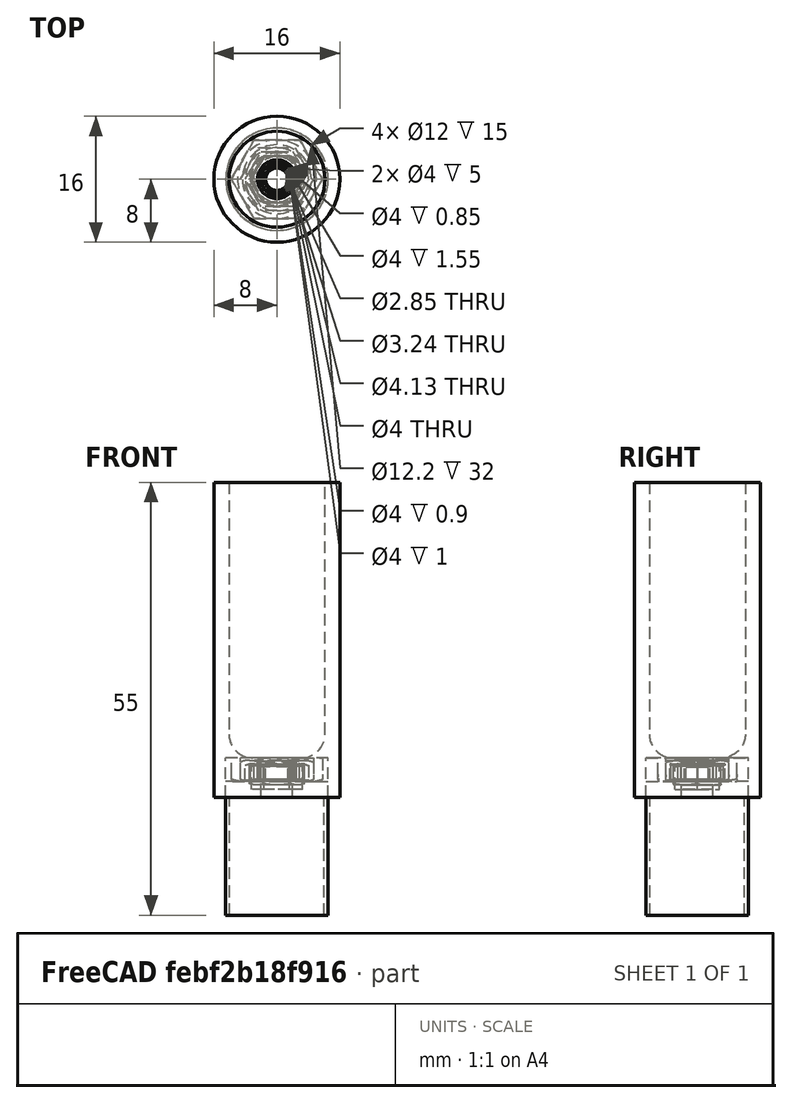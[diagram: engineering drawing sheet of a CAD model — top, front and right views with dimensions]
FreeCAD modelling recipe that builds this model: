
FCSTD DOCUMENT  (FreeCAD 0.20R29177 (Git))
Label: soporte
License: All rights reserved
LicenseURL: http://en.wikipedia.org/wiki/All_rights_reserved
objects: Part::Cylinder×24, Part::Cut×18, Part::FeaturePython×13, Part::MultiFuse×11, Mesh::Feature×6, Part::Prism×1, Part::Fillet×1
note: 68 computed .brp shape members not serialized (recipe doc carries the construction recipe); baked Part::Feature solids carry a one-line shape summary decoded from their .brp

FEATURE [Part::Cylinder] Cylinder
  Angle = 360
  AttacherType = Attacher::AttachEngine3D
  FirstAngle = 0
  Height = 15
  Radius = 6.5
  SecondAngle = 0
FEATURE [Part::Cylinder] Cylinder001
  Angle = 360
  AttacherType = Attacher::AttachEngine3D
  FirstAngle = 0
  Height = 15
  Radius = 6
  SecondAngle = 0
FEATURE [Part::Cut] Cut
  Base = -> Cylinder
  Placement = pos=(0,0,-15) rot=(0,0,1;0rad)
  Tool = -> Cylinder001
FEATURE [Part::Cylinder] Cylinder002
  Angle = 360
  AttacherType = Attacher::AttachEngine3D
  FirstAngle = 0
  Height = 5
  Radius = 6.5
  SecondAngle = 0
FEATURE [Part::Cylinder] Cylinder003
  Angle = 360
  AttacherType = Attacher::AttachEngine3D
  FirstAngle = 0
  Height = 10
  Radius = 2
  SecondAngle = 0
FEATURE [Part::Cut] Cut001
  Base = -> Cylinder002
  Tool = -> Cylinder003
FEATURE [Part::FeaturePython] Nut  label="(M3.5)-Nut"  # Fasteners workbench fastener (typed FeaturePython)
  Placement = pos=(0,0,2) rot=(0,0,1;0rad)
  diameter = 5
  invert = false
  leftHanded = false
  matchOuter = false
  offset = 0
  thread = false
  type = 11
FEATURE [Part::FeaturePython] Nut001  label="(M3.5)-Nut001"  # Fasteners workbench fastener (typed FeaturePython)
  Placement = pos=(0,0,2.6) rot=(0,0,1;0rad)
  diameter = 5
  invert = false
  leftHanded = false
  matchOuter = false
  offset = 0
  thread = false
  type = 11
FEATURE [Part::MultiFuse] Fusion
  Placement = pos=(0,0,-0.45) rot=(0,0,1;0rad)
  Shapes = -> [Nut,Nut001]
FEATURE [Part::Cut] Cut002
  Base = -> Cut001
  Tool = -> Fusion
FEATURE [Part::MultiFuse] Fusion001  label="soporte_m35"
  Shapes = -> [Cut,Cut002]
FEATURE [Part::FeaturePython] Nut002  label="M4-Nut"  # Fasteners workbench fastener (typed FeaturePython)
  Placement = pos=(0,0,2) rot=(0,0,1;0rad)
  diameter = 6
  invert = false
  leftHanded = false
  matchOuter = false
  offset = 0
  thread = false
  type = 11
FEATURE [Part::Cylinder] Cylinder004
  Angle = 360
  AttacherType = Attacher::AttachEngine3D
  FirstAngle = 0
  Height = 5
  Radius = 6.5
  SecondAngle = 0
FEATURE [Part::Cylinder] Cylinder005
  Angle = 360
  AttacherType = Attacher::AttachEngine3D
  FirstAngle = 0
  Height = 15
  Radius = 6.5
  SecondAngle = 0
FEATURE [Part::Cylinder] Cylinder006
  Angle = 360
  AttacherType = Attacher::AttachEngine3D
  FirstAngle = 0
  Height = 10
  Radius = 2
  SecondAngle = 0
FEATURE [Part::Cylinder] Cylinder007
  Angle = 360
  AttacherType = Attacher::AttachEngine3D
  FirstAngle = 0
  Height = 15
  Radius = 6
  SecondAngle = 0
FEATURE [Part::Cut] Cut003
  Base = -> Cylinder005
  Placement = pos=(0,0,-15) rot=(0,0,1;0rad)
  Tool = -> Cylinder007
FEATURE [Part::Cut] Cut005
  Base = -> Cylinder004
  Tool = -> Cylinder006
FEATURE [Part::FeaturePython] Nut003  label="M4-Nut001"  # Fasteners workbench fastener (typed FeaturePython)
  Placement = pos=(0,0,2.6) rot=(0,0,1;0rad)
  diameter = 6
  invert = false
  leftHanded = false
  matchOuter = false
  offset = 0
  thread = false
  type = 11
FEATURE [Part::MultiFuse] Fusion002
  Placement = pos=(0,0,-0.72) rot=(0,0,1;0rad)
  Shapes = -> [Nut002,Nut003]
FEATURE [Part::Cut] Cut004
  Base = -> Cut005
  Tool = -> Fusion002
FEATURE [Part::MultiFuse] Fusion003  label="soporte_m4"
  Shapes = -> [Cut003,Cut004]
FEATURE [Part::Cylinder] Cylinder008
  Angle = 360
  AttacherType = Attacher::AttachEngine3D
  FirstAngle = 0
  Height = 5
  Radius = 6.5
  SecondAngle = 0
FEATURE [Part::FeaturePython] Nut004  label="M5-Nut"  # Fasteners workbench fastener (typed FeaturePython)
  Placement = pos=(0,0,2) rot=(0,0,1;0rad)
  diameter = 7
  invert = false
  leftHanded = false
  matchOuter = false
  offset = 0
  thread = false
  type = 11
FEATURE [Part::FeaturePython] Nut005  label="M5-Nut001"  # Fasteners workbench fastener (typed FeaturePython)
  Placement = pos=(0,0,2.6) rot=(0,0,1;0rad)
  diameter = 7
  invert = false
  leftHanded = false
  matchOuter = false
  offset = 0
  thread = false
  type = 11
FEATURE [Part::MultiFuse] Fusion004
  Shapes = -> [Nut004,Nut005]
FEATURE [Part::Cylinder] Cylinder009
  Angle = 360
  AttacherType = Attacher::AttachEngine3D
  FirstAngle = 0
  Height = 10
  Radius = 2
  SecondAngle = 0
FEATURE [Part::Cut] Cut007
  Base = -> Cylinder008
  Tool = -> Cylinder009
FEATURE [Part::Cut] Cut008
  Base = -> Cut007
  Tool = -> Fusion004
FEATURE [Part::Cylinder] Cylinder010
  Angle = 360
  AttacherType = Attacher::AttachEngine3D
  FirstAngle = 0
  Height = 15
  Radius = 6.5
  SecondAngle = 0
FEATURE [Part::Cylinder] Cylinder011
  Angle = 360
  AttacherType = Attacher::AttachEngine3D
  FirstAngle = 0
  Height = 15
  Radius = 6
  SecondAngle = 0
FEATURE [Part::Cut] Cut006
  Base = -> Cylinder010
  Placement = pos=(0,0,-15) rot=(0,0,1;0rad)
  Tool = -> Cylinder011
FEATURE [Part::MultiFuse] Fusion005  label="soporte_m5"
  Shapes = -> [Cut006,Cut008]
FEATURE [Part::FeaturePython] Nut006  label="M6-Nut001"  # Fasteners workbench fastener (typed FeaturePython)
  Placement = pos=(0,0,2.6) rot=(0,0,1;0rad)
  diameter = 8
  invert = false
  leftHanded = false
  matchOuter = false
  offset = 0
  thread = false
  type = 11
FEATURE [Part::FeaturePython] Nut007  label="M6-Nut"  # Fasteners workbench fastener (typed FeaturePython)
  Placement = pos=(0,0,2) rot=(0,0,1;0rad)
  diameter = 8
  invert = false
  leftHanded = false
  matchOuter = false
  offset = 0
  thread = false
  type = 11
FEATURE [Part::MultiFuse] Fusion006
  Shapes = -> [Nut007,Nut006]
FEATURE [Part::Cylinder] Cylinder012
  Angle = 360
  AttacherType = Attacher::AttachEngine3D
  FirstAngle = 0
  Height = 5
  Radius = 6.5
  SecondAngle = 0
FEATURE [Part::Cylinder] Cylinder013
  Angle = 360
  AttacherType = Attacher::AttachEngine3D
  FirstAngle = 0
  Height = 10
  Radius = 2
  SecondAngle = 0
FEATURE [Part::Cut] Cut011
  Base = -> Cylinder012
  Tool = -> Cylinder013
FEATURE [Part::Cut] Cut009
  Base = -> Cut011
  Tool = -> Fusion006
FEATURE [Part::Cylinder] Cylinder014
  Angle = 360
  AttacherType = Attacher::AttachEngine3D
  FirstAngle = 0
  Height = 15
  Radius = 6.5
  SecondAngle = 0
FEATURE [Part::Cylinder] Cylinder015
  Angle = 360
  AttacherType = Attacher::AttachEngine3D
  FirstAngle = 0
  Height = 15
  Radius = 6
  SecondAngle = 0
FEATURE [Part::Cut] Cut010
  Base = -> Cylinder014
  Placement = pos=(0,0,-15) rot=(0,0,1;0rad)
  Tool = -> Cylinder015
FEATURE [Part::MultiFuse] Fusion007  label="soporte_m6"
  Shapes = -> [Cut010,Cut009]
FEATURE [Part::FeaturePython] Nut008  label="M8-Nut001"  # Fasteners workbench fastener (typed FeaturePython)
  Placement = pos=(0,0,2.6) rot=(0,0,1;0rad)
  diameter = 9
  invert = false
  leftHanded = false
  matchOuter = false
  offset = 0
  thread = false
  type = 11
FEATURE [Part::FeaturePython] Nut009  label="M8-Nut"  # Fasteners workbench fastener (typed FeaturePython)
  Placement = pos=(0,0,2) rot=(0,0,1;0rad)
  diameter = 9
  invert = false
  leftHanded = false
  matchOuter = false
  offset = 0
  thread = false
  type = 11
FEATURE [Part::MultiFuse] Fusion009
  Shapes = -> [Nut009,Nut008]
FEATURE [Part::Cylinder] Cylinder016
  Angle = 360
  AttacherType = Attacher::AttachEngine3D
  FirstAngle = 0
  Height = 15
  Radius = 6
  SecondAngle = 0
FEATURE [Part::Cylinder] Cylinder017
  Angle = 360
  AttacherType = Attacher::AttachEngine3D
  FirstAngle = 0
  Height = 5
  Radius = 6.5
  SecondAngle = 0
FEATURE [Part::Cylinder] Cylinder018
  Angle = 360
  AttacherType = Attacher::AttachEngine3D
  FirstAngle = 0
  Height = 10
  Radius = 2
  SecondAngle = 0
FEATURE [Part::Cut] Cut014
  Base = -> Cylinder017
  Tool = -> Cylinder018
FEATURE [Part::Cut] Cut012
  Base = -> Cut014
  Tool = -> Fusion009
FEATURE [Part::Cylinder] Cylinder019
  Angle = 360
  AttacherType = Attacher::AttachEngine3D
  FirstAngle = 0
  Height = 15
  Radius = 6.5
  SecondAngle = 0
FEATURE [Part::Cut] Cut013
  Base = -> Cylinder019
  Placement = pos=(0,0,-15) rot=(0,0,1;0rad)
  Tool = -> Cylinder016
FEATURE [Part::MultiFuse] Fusion008  label="soporte_m8"
  Shapes = -> [Cut013,Cut012]
FEATURE [Mesh::Feature] Mesh002  label="soporte_m_5"
FEATURE [Mesh::Feature] Mesh003  label="soporte_m_6"
FEATURE [Mesh::Feature] Mesh004  label="soporte_m_8"
FEATURE [Mesh::Feature] Mesh005  label="soporte_m_35"
FEATURE [Mesh::Feature] Mesh  label="soporte_m_4"
FEATURE [Part::FeaturePython] Nut010  label="M4-Nut002"  # Fasteners workbench fastener (typed FeaturePython)
  Placement = pos=(0,0,2) rot=(0,0,1;0rad)
  diameter = 6
  invert = false
  leftHanded = false
  matchOuter = false
  offset = 0
  thread = false
  type = 11
FEATURE [Part::FeaturePython] Nut011  label="(M3.5)-Nut002"  # Fasteners workbench fastener (typed FeaturePython)
  Placement = pos=(0,0,2) rot=(0,0,1;0rad)
  diameter = 5
  invert = false
  leftHanded = false
  matchOuter = false
  offset = 0
  thread = false
  type = 11
FEATURE [Part::FeaturePython] Nut012  label="M5-Nut002"  # Fasteners workbench fastener (typed FeaturePython)
  Placement = pos=(0,0,2) rot=(0,0,1;0rad)
  diameter = 7
  invert = false
  leftHanded = false
  matchOuter = false
  offset = 0
  thread = false
  type = 11
FEATURE [Part::Prism] Prism
  AttacherType = Attacher::AttachEngine3D
  Circumradius = 3.25
  FirstAngle = 0
  Height = 3.1
  Placement = pos=(0,0,1) rot=(0,0,1;0rad)
  Polygon = 6
  SecondAngle = 0
FEATURE [Part::Cylinder] Cylinder020
  Angle = 360
  AttacherType = Attacher::AttachEngine3D
  FirstAngle = 0
  Height = 5
  Radius = 8
  SecondAngle = 0
FEATURE [Part::Cylinder] Cylinder021
  Angle = 360
  AttacherType = Attacher::AttachEngine3D
  FirstAngle = 0
  Height = 10
  Radius = 2
  SecondAngle = 0
FEATURE [Part::Cut] Cut015
  Base = -> Cylinder020
  Tool = -> Cylinder021
FEATURE [Part::Cylinder] Cylinder022
  Angle = 360
  AttacherType = Attacher::AttachEngine3D
  FirstAngle = 0
  Height = 35
  Radius = 8
  SecondAngle = 0
FEATURE [Part::Cylinder] Cylinder023
  Angle = 360
  AttacherType = Attacher::AttachEngine3D
  FirstAngle = 0
  Height = 35
  Radius = 6.1
  SecondAngle = 0
FEATURE [Part::Cut] Cut016
  Base = -> Cylinder022
  Placement = pos=(0,0,5) rot=(0,0,1;0rad)
  Tool = -> Cylinder023
FEATURE [Part::Cut] Cut017
  Base = -> Cut015
  Tool = -> Prism
FEATURE [Part::MultiFuse] Fusion010  label="soporte_prisma_radio_325"
  Shapes = -> [Cut016,Cut017]
FEATURE [Part::Fillet] Fillet
  Base = -> Fusion010
  Edges = 1 edges r=3: [Edge9]
FEATURE [Mesh::Feature] Mesh006  label="Fillet (Meshed)"
